# Revit family: 51911183
name_source: partatom
category: Plumbing Fixtures
revit_build: Autodesk Revit 2018 (Build: 20170223_1515(x64)
units: mm (PartAtom-declared; Revit-internal decimal feet)

## family parameters
Always vertical = Yes
Cut with Voids When Loaded = No
OmniClass Number = 23.45.55.00
OmniClass Title = Sanitary Faucets, Wastes
Part Type = Normal
Room Calculation Point = No
Round Connector Dimension = Use Diameter
Shared = No
Work Plane-Based = No

## types (1)
- 51911183 Washbasin faucet, low pressure
    2D/3D/BIM Files URL = http://static.hansa.com
    3D View = https://static.hansa.com
    Advanced Features = Inner body made of DZR brass;3S-installation system for safe and simple mounting
    Aerator = Laminar stream;Standard aerator
    AssetType = Fixed
    BIMObjectName = 51911183
    Backflow Prevention EN1717 = AA
    BodyMaterial = Brass
    Brand = HANSA
    Catalog Drawing URL = http://static.hansa.com
    Category = Bathroom
    CloseOffRating = 0
    Color = Chrome
    Connection = Flexible inlet pipes
    Connection Size = G3/8
    Dimension Drawing URL = http://static.hansa.com
    DurationUnit = Year
    EAN Number = 4057304007545
    EN Standard = EN 817
    ETIM Class Number = EC011328 Washbasin mixing tap
    Extensions = Pop-up waste with draw-rod
    FDV Document URL = http://www.hansa.com
    FaucetMainMaterial = Brass
    Features = Single-lever;Low pressure
    Finish = Polished
    Flow Drawing URL = http://static.hansa.com
    Flow Rate At 300kPa With Flow Controller = 0.0 L/s
    FlowCoefficient = 0
    Group = Washbasin faucet
    IfcExportAs = IfcValveType
    IfcExportType = FAUCET
    InletConnectionSize = 10 mm  [stored 0.0328084 ft]
    Installation Type = Deck mounted
    Installation and Maintenance Guide URL = http://static.hansa.com
    Interactive AR View URL = https://static.hansa.com
    Lever Handle = Hot/Cold symbols;Single operating lever/handle
    Manufacturer = HANSA
    ManufacturerName = HANSA
    ManufacturerURL = http://www.hansa.com
    Market = International;Germany;Austria;Belgium;Netherlands;Czech Republic;Slovakia
    Material = Brass
    Max. Hot Water Supply = 70 °C
    Mechanical Parts = ø 40 mm ceramic cartridge for flow and temperature control
    Mobile Product Information URL = http://mpi.hansa.com
    Model = 51911183 Washbasin faucet, low pressure
    ModelReference = 51911183
    Mounting Holes = 1 hole
    NBSDescription = Water supply fittings for wash basins and troughs
    NBSReference = 45-35-70/371
    Name = 51911183 Washbasin faucet, low pressure
    Name_en = 51911183 Washbasin faucet, low pressure
    Noise Class = I (ISO 3822)
    NominalDepth = 174 mm  [stored 0.570866 ft]
    NominalHeight = 170 mm  [stored 0.557743 ft]
    NominalWidth = 49 mm
    Product Code = 51911183
    Product Family = HANSADESIGNO Style
    Product Image URL = http://static.hansa.com
    Product URL = http://static.hansa.com
    Revision = 4
    Sales Package dimensions (LxWxH) = 380 x 180 x 74
    Shape = Sculptured
    Short Marketing = one-hole single-lever basin mixer, DN 15
    Size = 50x175x170 mm
    Spare-Part Information URL = http://static.hansa.com
    Spout Projection = 119 mm
    Spout Type = Fixed spout
    Surface treatment = Chrome
    Technical DataSheet URL = http://www.hansa.com
    UNSPSC Class Number = 30181700 Faucets or taps
    URL Declaration of Conformity = http://static.hansa.com
    URL REACH = http://static.hansa.com
    Uniclass2 = Pr_40_30_96_96
    Uniclass2015Description = Washbasin manual water supply sets
    Uniclass2015Reference = Pr_40_20_87_96
    Version = 4
    VersionDate = 01/07/2022
    Warranty Information URL = http://warranty.hansa.com
    WarrantyDescription = http://warranty.hansa.com
    WarrantyDurationUnit = Year
    Working Pressure = 50 - 500 kPa
    WorkingPressure = 50 - 500 kPa

note: [stored X ft] marks values corroborated as IEEE doubles in the binary element streams (Revit-internal decimal feet)

## geometry (parser evidence)
native form markers: Sweep x5
no freeform markers — native parametric forms only
